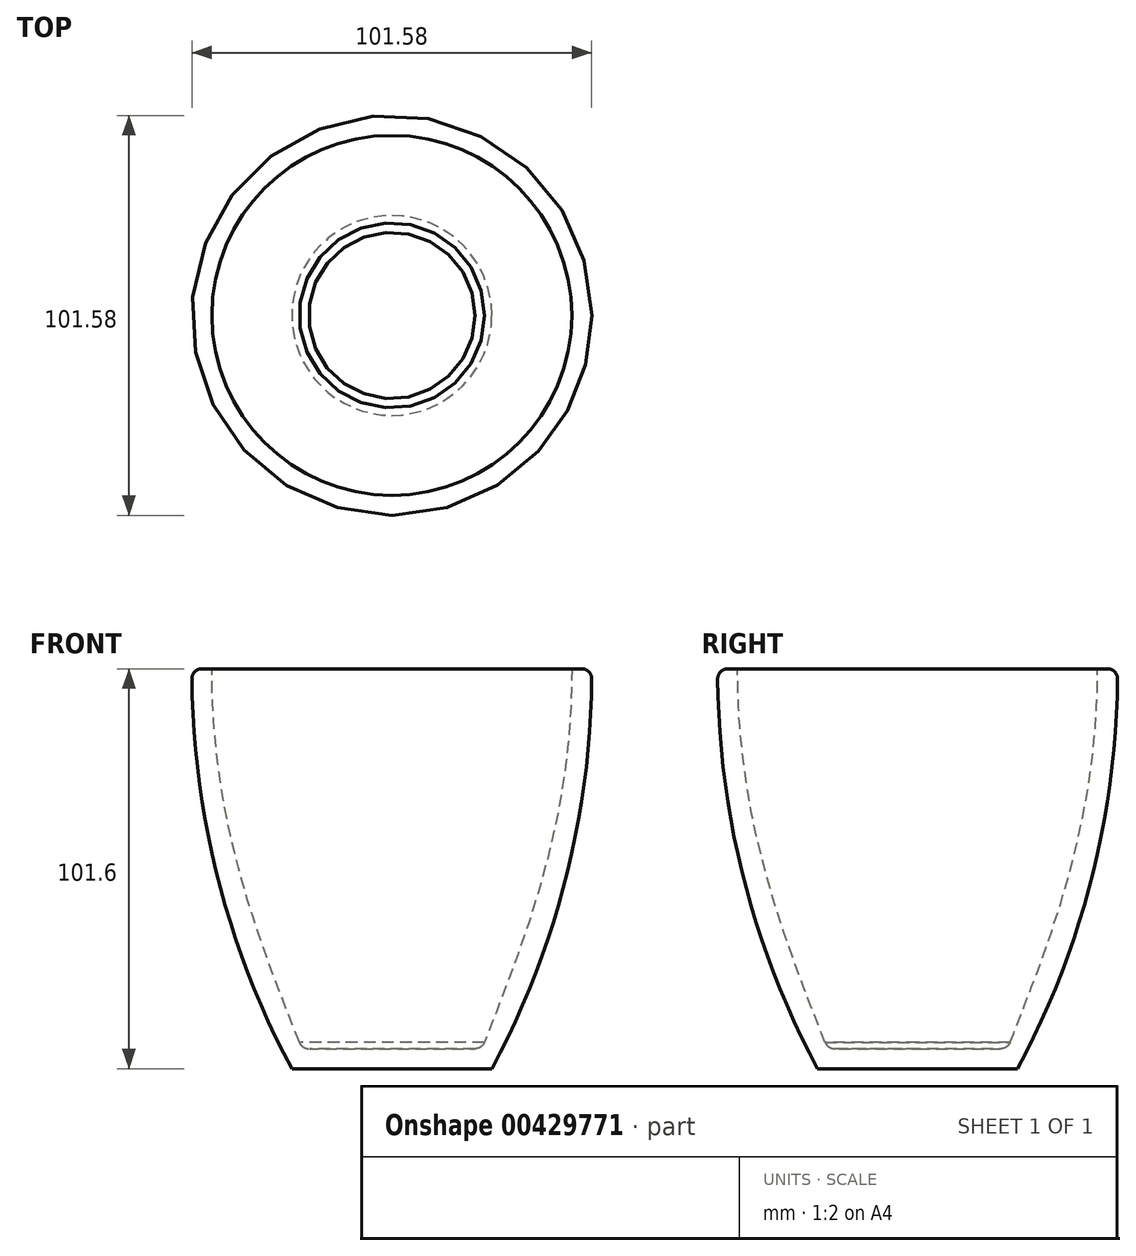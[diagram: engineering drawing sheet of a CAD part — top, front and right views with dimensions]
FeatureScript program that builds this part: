
annotation { "Feature Type Name" : "Feature", "Feature Type Description" : "" }
export const myFeature = defineFeature(function(context is Context, id is Id, definition is map)
    precondition{}
    {
        {
            var Q0;
            Q0=qCreatedBy(makeId("Top.planeOp"),FACE);
            var sketch = newSketch(context, id + "F0", { "sketchPlane" : qUnion([Q0])});
            skCircle(sketch, "E0", {"center": v(0, 0) * mm, "radius": 25.4 * mm});
            skSolve(sketch);
        }
        {
            var Q0;
            Q0=qCreatedBy(makeId("Top.planeOp"),FACE);
            cPlane(context, id + "F1", {"entities" : qUnion([Q0]), "cplaneType" : CPlaneType.OFFSET, "offset" : 101.6 * mm, "width" : 152.4 * mm, "height" : 152.4 * mm});
        }
        {
            var Q0;
            Q0=qCreatedBy(id+"F1.planeOp",FACE);
            var sketch = newSketch(context, id + "F2", { "sketchPlane" : qUnion([Q0])});
            skCircle(sketch, "E1", {"center": v(0, 0) * mm, "radius": 50.8 * mm});
            skSolve(sketch);
        }
        {
            var Q0;
            Q0=qCreatedBy(makeId("Front.planeOp"),FACE);
            var sketch = newSketch(context, id + "F3", { "sketchPlane" : qUnion([Q0])});
            skArc(sketch, "E2", {"start": v(25.4, 0) * mm, "mid": v(44.41, 49.22) * mm, "end": v(50.8, 101.6) * mm});
            skSolve(sketch);
        }
        {
            var Q0;
            Q0=makeQuery(id+"F2.imprint","IMPRINT",FACE,{"disambiguationData":[TD([[makeQuery(id+"F2.imprint","IMPRINT",EDGE,{"derivedFrom":sQuery(id+"F2.wireOp",EDGE,"E1")}),1.0]])]});
            var Q1;
            Q1=makeQuery(id+"F0.imprint","IMPRINT",FACE,{"disambiguationData":[TD([[makeQuery(id+"F0.imprint","IMPRINT",EDGE,{"derivedFrom":sQuery(id+"F0.wireOp",EDGE,"E0")}),1.0]])]});
            var Q2;
            Q2=sQuery(id+"F3.wireOp",EDGE,"E2");
            loft(context, id + "F4", {"addGuides" : true, "sheetProfilesArray" : [{ "sheetProfileEntities" : qUnion([Q0]) }, { "sheetProfileEntities" : qUnion([Q1]) }], "guidesArray" : [{ "guideEntities" : qUnion([Q2]), "guideDerivativeType" : LoftGuideDerivativeType.DEFAULT, "guideDerivativeMagnitude" : 1 }]});
        }
        {
            var Q0;
            Q0=makeQuery(id+"F4.opLoft","CAP_FACE",FACE,{"disambiguationData":[OSD([makeQuery(id+"F2.imprint","IMPRINT",FACE,{"disambiguationData":[TD([[makeQuery(id+"F2.imprint","IMPRINT",EDGE,{"derivedFrom":sQuery(id+"F2.wireOp",EDGE,"E1")}),1.0]])]})])],"isStart":true});
            var sketch = newSketch(context, id + "F5", { "sketchPlane" : qUnion([Q0])});
            skCircle(sketch, "E3", {"center": v(0, 0) * mm, "radius": 45.72 * mm});
            skSolve(sketch);
        }
        {
            var Q0;
            Q0=qCreatedBy(makeId("Top.planeOp"),FACE);
            cPlane(context, id + "F6", {"entities" : qUnion([Q0]), "cplaneType" : CPlaneType.OFFSET, "offset" : 5.08 * mm, "width" : 152.4 * mm, "height" : 152.4 * mm});
        }
        {
            var Q0;
            Q0=qCreatedBy(id+"F6.planeOp",FACE);
            var sketch = newSketch(context, id + "F7", { "sketchPlane" : qUnion([Q0])});
            skCircle(sketch, "E4", {"center": v(0, 0) * mm, "radius": 22.86 * mm});
            skSolve(sketch);
        }
        {
            var Q1;
            Q1 = qSketchRegion(id + "F5", true);
            var Q2;
            Q2 = qSketchRegion(id + "F7", true);
            loft(context, id + "F8", {"operationType" : NewBodyOperationType.REMOVE, "startCondition" : LoftEndDerivativeType.NORMAL_TO_PROFILE, "startMagnitude" : 1.2, "sheetProfilesArray" : [{ "sheetProfileEntities" : qUnion([Q1]) }, { "sheetProfileEntities" : qUnion([Q2]) }]});
        }
        {
            var Q0;
            Q0=makeQuery(id+"F8.boolean.opBoolean","COPY",EDGE,{"derivedFrom":makeQuery(id+"F8.opLoft","MID_CAP_EDGE",EDGE,{"disambiguationData":[OSD([sQuery(id+"F5.wireOp",EDGE,"E3"),sQuery(id+"F7.wireOp",EDGE,"E4")])],"capPos":1.0})});
            var Q1;
            Q1=makeQuery(id+"F8.boolean.opBoolean","COPY",EDGE,{"derivedFrom":makeQuery(id+"F8.opLoft","MID_CAP_EDGE",EDGE,{"disambiguationData":[OSD([sQuery(id+"F5.wireOp",EDGE,"E3")])],"capPos":0.0})});
            var Q2;
            Q2=makeQuery(id+"F4.opLoft","MID_CAP_EDGE",EDGE,{"disambiguationData":[OSD([sQuery(id+"F2.wireOp",EDGE,"E1"),sQuery(id+"F3.wireOp",EDGE,"E2")])],"capPos":0.0});
            fillet(context, id + "F9", {"entities" : qUnion([Q0, Q1, Q2]), "radius" : 2.54 * mm, "tangentPropagation" : true, "allowEdgeOverflow" : false});
        }
    });
